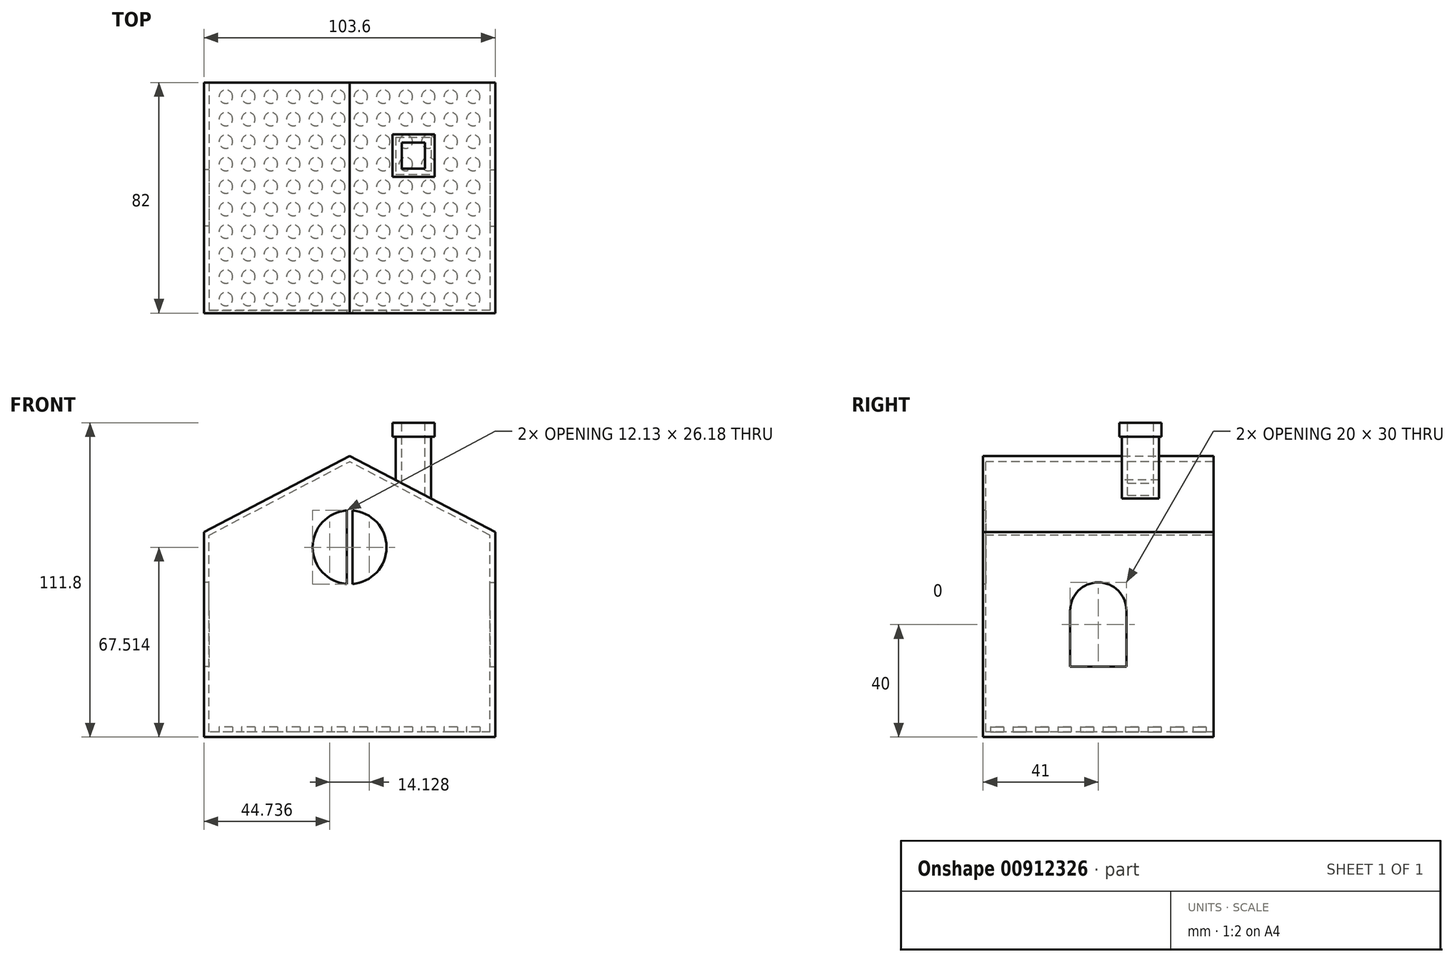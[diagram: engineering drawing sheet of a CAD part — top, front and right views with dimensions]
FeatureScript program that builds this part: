
annotation { "Feature Type Name" : "Feature", "Feature Type Description" : "" }
export const myFeature = defineFeature(function(context is Context, id is Id, definition is map)
    precondition{}
    {
        {
            var Q0;
            Q0=qCreatedBy(makeId("Front.planeOp"),FACE);
            var sketch = newSketch(context, id + "F0", { "sketchPlane" : qUnion([Q0])});
            skLineSegment(sketch, "E0", {"start": v(0, 0) * mm, "end": v(50, 0) * mm});
            skLineSegment(sketch, "E1", {"start": v(50, 0) * mm, "end": v(50, 70) * mm});
            skLineSegment(sketch, "E2", {"start": v(50, 70) * mm, "end": v(0, 96.17) * mm});
            skLineSegment(sketch, "E3", {"start": v(0, 96.17) * mm, "end": v(0, 0) * mm, "construction": true});
            skLineSegment(sketch, "E4.MirrorCS", {"start": v(-50, 70) * mm, "end": v(0, 96.17) * mm});
            skLineSegment(sketch, "E5.MirrorCS", {"start": v(-50, 0) * mm, "end": v(-50, 70) * mm});
            skLineSegment(sketch, "E6.MirrorCS", {"start": v(0, 0) * mm, "end": v(-50, 0) * mm});
            skLineSegment(sketch, "E7.0", {"start": v(0, -1.8) * mm, "end": v(51.8, -1.8) * mm});
            skLineSegment(sketch, "E7.1", {"start": v(51.8, 71.09) * mm, "end": v(0, 98.2) * mm});
            skLineSegment(sketch, "E7.2", {"start": v(-51.8, 71.09) * mm, "end": v(0, 98.2) * mm});
            skLineSegment(sketch, "E7.3", {"start": v(51.8, -1.8) * mm, "end": v(51.8, 71.09) * mm});
            skLineSegment(sketch, "E7.4", {"start": v(-51.8, -1.8) * mm, "end": v(-51.8, 71.09) * mm});
            skLineSegment(sketch, "E7.5", {"start": v(0, -1.8) * mm, "end": v(-51.8, -1.8) * mm});
            skSolve(sketch);
        }
        {
            var Q0;
            Q0=makeQuery(id+"F0.imprint","IMPRINT",FACE,{"disambiguationData":[TD([[makeQuery(id+"F0.imprint","IMPRINT",EDGE,{"derivedFrom":sQuery(id+"F0.wireOp",EDGE,"E0")}),-1.0]])]});
            var Q1;
            Q1=makeQuery(id+"F0.imprint","IMPRINT",FACE,{"disambiguationData":[TD([[makeQuery(id+"F0.imprint","IMPRINT",EDGE,{"derivedFrom":sQuery(id+"F0.wireOp",EDGE,"E0")}),1.0]])]});
            extrude(context, id + "F1", {"entities" : qUnion([Q0, Q1]), "endBound" : BoundingType.SYMMETRIC, "depth" : 82 * mm, "offsetDistance" : 25 * mm});
        }
        {
            var Q0;
            Q0=makeQuery(id+"F1.opExtrude","SWEPT_FACE",FACE,{"disambiguationData":[OSD([sQuery(id+"F0.wireOp",EDGE,"E7.4")])]});
            var sketch = newSketch(context, id + "F2", { "sketchPlane" : qUnion([Q0])});
            skLineSegment(sketch, "E8.top", {"start": v(-10, 23.2) * mm, "end": v(10, 23.2) * mm});
            skLineSegment(sketch, "E8.left", {"start": v(-10, 43.2) * mm, "end": v(-10, 23.2) * mm});
            skLineSegment(sketch, "E8.right", {"start": v(10, 43.2) * mm, "end": v(10, 23.2) * mm});
            skArc(sketch, "E9", {"start": v(10, 43.2) * mm, "mid": v(0, 53.2) * mm, "end": v(-10, 43.2) * mm});
            skSolve(sketch);
        }
        {
            var Q0;
            Q0=makeQuery(id+"F2.imprint","IMPRINT",FACE,{"disambiguationData":[TD([[makeQuery(id+"F2.imprint","IMPRINT",EDGE,{"derivedFrom":sQuery(id+"F2.wireOp",EDGE,"E8.bottom")}),-1.0]])]});
            var Q1;
            Q1=makeQuery(id+"F2.imprint","IMPRINT",FACE,{"disambiguationData":[TD([[makeQuery(id+"F2.imprint","IMPRINT",EDGE,{"derivedFrom":sQuery(id+"F2.wireOp",EDGE,"E8.top")}),1.0]])]});
            extrude(context, id + "F3", {"entities" : qUnion([Q0, Q1]), "operationType" : NewBodyOperationType.REMOVE, "oppositeDirection" : true, "depth" : 25 * mm, "offsetDistance" : 25 * mm});
        }
        {
            var Q0;
            Q0=makeQuery(id+"F1.opExtrude","SWEPT_FACE",FACE,{"disambiguationData":[OSD([sQuery(id+"F0.wireOp",EDGE,"E7.3")])]});
            var sketch = newSketch(context, id + "F4", { "sketchPlane" : qUnion([Q0])});
            skLineSegment(sketch, "E10.top", {"start": v(-10, 23.2) * mm, "end": v(10, 23.2) * mm});
            skLineSegment(sketch, "E10.left", {"start": v(-10, 43.2) * mm, "end": v(-10, 23.2) * mm});
            skLineSegment(sketch, "E10.right", {"start": v(10, 43.2) * mm, "end": v(10, 23.2) * mm});
            skArc(sketch, "E11", {"start": v(10, 43.2) * mm, "mid": v(0, 53.2) * mm, "end": v(-10, 43.2) * mm});
            skSolve(sketch);
        }
        {
            var Q0;
            Q0=makeQuery(id+"F4.imprint","IMPRINT",FACE,{"disambiguationData":[TD([[makeQuery(id+"F4.imprint","IMPRINT",EDGE,{"derivedFrom":sQuery(id+"F4.wireOp",EDGE,"E10.top")}),1.0]])]});
            extrude(context, id + "F5", {"entities" : qUnion([Q0]), "operationType" : NewBodyOperationType.REMOVE, "oppositeDirection" : true, "depth" : 25 * mm, "offsetDistance" : 25 * mm});
        }
        {
            var Q0;
            Q0=qCreatedBy(makeId("Front.planeOp"),FACE);
            cPlane(context, id + "F6", {"entities" : qUnion([Q0]), "cplaneType" : CPlaneType.OFFSET, "offset" : 40 * mm, "width" : 150 * mm, "height" : 150 * mm});
        }
        {
            var Q0;
            Q0=makeQuery(id+"F0.imprint","IMPRINT",FACE,{"disambiguationData":[TD([[makeQuery(id+"F0.imprint","IMPRINT",EDGE,{"derivedFrom":sQuery(id+"F0.wireOp",EDGE,"E0")}),1.0]])]});
            extrude(context, id + "F7", {"entities" : qUnion([Q0]), "operationType" : NewBodyOperationType.REMOVE, "oppositeDirection" : true, "depth" : 41 * mm, "offsetDistance" : 25 * mm});
        }
        {
            var Q0;
            Q0=makeQuery(id+"F0.imprint","IMPRINT",FACE,{"disambiguationData":[TD([[makeQuery(id+"F0.imprint","IMPRINT",EDGE,{"derivedFrom":sQuery(id+"F0.wireOp",EDGE,"E0")}),1.0]])]});
            extrude(context, id + "F8", {"entities" : qUnion([Q0]), "operationType" : NewBodyOperationType.REMOVE, "depth" : 40 * mm, "offsetDistance" : 25 * mm});
        }
        {
            var Q0;
            Q0=makeQuery(id+"F1.opExtrude","CAP_FACE",FACE,{"disambiguationData":[OSD([sQuery(id+"F0.wireOp",EDGE,"E7.0"),sQuery(id+"F0.wireOp",EDGE,"E7.1"),sQuery(id+"F0.wireOp",EDGE,"E7.2"),sQuery(id+"F0.wireOp",EDGE,"E7.3"),sQuery(id+"F0.wireOp",EDGE,"E7.4"),sQuery(id+"F0.wireOp",EDGE,"E7.5")])],"isStart":false});
            var sketch = newSketch(context, id + "F9", { "sketchPlane" : qUnion([Q0])});
            skCircle(sketch, "E12", {"center": v(0, 65.71) * mm, "radius": 13.13 * mm});
            skLineSegment(sketch, "E13", {"start": v(-13.13, 65.96) * mm, "end": v(13.13, 65.96) * mm, "construction": true});
            skLineSegment(sketch, "E14", {"start": v(0, 78.84) * mm, "end": v(0, 52.59) * mm, "construction": true});
            skLineSegment(sketch, "E15.0", {"start": v(-1, 78.84) * mm, "end": v(-1, 52.59) * mm});
            skLineSegment(sketch, "E16.0", {"start": v(1, 78.84) * mm, "end": v(1, 52.59) * mm});
            skSolve(sketch);
        }
        {
            var Q0;
            Q0=qCreatedBy(makeId("Top.planeOp"),FACE);
            var sketch = newSketch(context, id + "F10", { "sketchPlane" : qUnion([Q0])});
            skCircle(sketch, "E17", {"center": v(-44, 36) * mm, "radius": 2.4 * mm});
            skCircle(sketch, "E18.0.1.0", {"center": v(-44, 28) * mm, "radius": 2.4 * mm});
            skCircle(sketch, "E18.0.2.0", {"center": v(-44, 20) * mm, "radius": 2.4 * mm});
            skCircle(sketch, "E18.0.3.0", {"center": v(-44, 12) * mm, "radius": 2.4 * mm});
            skCircle(sketch, "E18.0.4.0", {"center": v(-44, 4) * mm, "radius": 2.4 * mm});
            skCircle(sketch, "E18.0.5.0", {"center": v(-44, -4) * mm, "radius": 2.4 * mm});
            skCircle(sketch, "E18.0.6.0", {"center": v(-44, -12) * mm, "radius": 2.4 * mm});
            skCircle(sketch, "E18.0.7.0", {"center": v(-44, -20) * mm, "radius": 2.4 * mm});
            skCircle(sketch, "E18.0.8.0", {"center": v(-44, -28) * mm, "radius": 2.4 * mm});
            skCircle(sketch, "E18.0.9.0", {"center": v(-44, -36) * mm, "radius": 2.4 * mm});
            skCircle(sketch, "E18.1.0.0", {"center": v(-36, 36) * mm, "radius": 2.4 * mm});
            skCircle(sketch, "E18.1.1.0", {"center": v(-36, 28) * mm, "radius": 2.4 * mm});
            skCircle(sketch, "E18.1.2.0", {"center": v(-36, 20) * mm, "radius": 2.4 * mm});
            skCircle(sketch, "E18.1.3.0", {"center": v(-36, 12) * mm, "radius": 2.4 * mm});
            skCircle(sketch, "E18.1.4.0", {"center": v(-36, 4) * mm, "radius": 2.4 * mm});
            skCircle(sketch, "E18.1.5.0", {"center": v(-36, -4) * mm, "radius": 2.4 * mm});
            skCircle(sketch, "E18.1.6.0", {"center": v(-36, -12) * mm, "radius": 2.4 * mm});
            skCircle(sketch, "E18.1.7.0", {"center": v(-36, -20) * mm, "radius": 2.4 * mm});
            skCircle(sketch, "E18.1.8.0", {"center": v(-36, -28) * mm, "radius": 2.4 * mm});
            skCircle(sketch, "E18.1.9.0", {"center": v(-36, -36) * mm, "radius": 2.4 * mm});
            skCircle(sketch, "E18.2.0.0", {"center": v(-28, 36) * mm, "radius": 2.4 * mm});
            skCircle(sketch, "E18.2.1.0", {"center": v(-28, 28) * mm, "radius": 2.4 * mm});
            skCircle(sketch, "E18.2.2.0", {"center": v(-28, 20) * mm, "radius": 2.4 * mm});
            skCircle(sketch, "E18.2.3.0", {"center": v(-28, 12) * mm, "radius": 2.4 * mm});
            skCircle(sketch, "E18.2.4.0", {"center": v(-28, 4) * mm, "radius": 2.4 * mm});
            skCircle(sketch, "E18.2.5.0", {"center": v(-28, -4) * mm, "radius": 2.4 * mm});
            skCircle(sketch, "E18.2.6.0", {"center": v(-28, -12) * mm, "radius": 2.4 * mm});
            skCircle(sketch, "E18.2.7.0", {"center": v(-28, -20) * mm, "radius": 2.4 * mm});
            skCircle(sketch, "E18.2.8.0", {"center": v(-28, -28) * mm, "radius": 2.4 * mm});
            skCircle(sketch, "E18.2.9.0", {"center": v(-28, -36) * mm, "radius": 2.4 * mm});
            skCircle(sketch, "E18.3.0.0", {"center": v(-20, 36) * mm, "radius": 2.4 * mm});
            skCircle(sketch, "E18.3.1.0", {"center": v(-20, 28) * mm, "radius": 2.4 * mm});
            skCircle(sketch, "E18.3.2.0", {"center": v(-20, 20) * mm, "radius": 2.4 * mm});
            skCircle(sketch, "E18.3.3.0", {"center": v(-20, 12) * mm, "radius": 2.4 * mm});
            skCircle(sketch, "E18.3.4.0", {"center": v(-20, 4) * mm, "radius": 2.4 * mm});
            skCircle(sketch, "E18.3.5.0", {"center": v(-20, -4) * mm, "radius": 2.4 * mm});
            skCircle(sketch, "E18.3.6.0", {"center": v(-20, -12) * mm, "radius": 2.4 * mm});
            skCircle(sketch, "E18.3.7.0", {"center": v(-20, -20) * mm, "radius": 2.4 * mm});
            skCircle(sketch, "E18.3.8.0", {"center": v(-20, -28) * mm, "radius": 2.4 * mm});
            skCircle(sketch, "E18.3.9.0", {"center": v(-20, -36) * mm, "radius": 2.4 * mm});
            skCircle(sketch, "E18.4.0.0", {"center": v(-12, 36) * mm, "radius": 2.4 * mm});
            skCircle(sketch, "E18.4.1.0", {"center": v(-12, 28) * mm, "radius": 2.4 * mm});
            skCircle(sketch, "E18.4.2.0", {"center": v(-12, 20) * mm, "radius": 2.4 * mm});
            skCircle(sketch, "E18.4.3.0", {"center": v(-12, 12) * mm, "radius": 2.4 * mm});
            skCircle(sketch, "E18.4.4.0", {"center": v(-12, 4) * mm, "radius": 2.4 * mm});
            skCircle(sketch, "E18.4.5.0", {"center": v(-12, -4) * mm, "radius": 2.4 * mm});
            skCircle(sketch, "E18.4.6.0", {"center": v(-12, -12) * mm, "radius": 2.4 * mm});
            skCircle(sketch, "E18.4.7.0", {"center": v(-12, -20) * mm, "radius": 2.4 * mm});
            skCircle(sketch, "E18.4.8.0", {"center": v(-12, -28) * mm, "radius": 2.4 * mm});
            skCircle(sketch, "E18.4.9.0", {"center": v(-12, -36) * mm, "radius": 2.4 * mm});
            skCircle(sketch, "E18.5.0.0", {"center": v(-4, 36) * mm, "radius": 2.4 * mm});
            skCircle(sketch, "E18.5.1.0", {"center": v(-4, 28) * mm, "radius": 2.4 * mm});
            skCircle(sketch, "E18.5.2.0", {"center": v(-4, 20) * mm, "radius": 2.4 * mm});
            skCircle(sketch, "E18.5.3.0", {"center": v(-4, 12) * mm, "radius": 2.4 * mm});
            skCircle(sketch, "E18.5.4.0", {"center": v(-4, 4) * mm, "radius": 2.4 * mm});
            skCircle(sketch, "E18.5.5.0", {"center": v(-4, -4) * mm, "radius": 2.4 * mm});
            skCircle(sketch, "E18.5.6.0", {"center": v(-4, -12) * mm, "radius": 2.4 * mm});
            skCircle(sketch, "E18.5.7.0", {"center": v(-4, -20) * mm, "radius": 2.4 * mm});
            skCircle(sketch, "E18.5.8.0", {"center": v(-4, -28) * mm, "radius": 2.4 * mm});
            skCircle(sketch, "E18.5.9.0", {"center": v(-4, -36) * mm, "radius": 2.4 * mm});
            skCircle(sketch, "E18.6.0.0", {"center": v(4, 36) * mm, "radius": 2.4 * mm});
            skCircle(sketch, "E18.6.1.0", {"center": v(4, 28) * mm, "radius": 2.4 * mm});
            skCircle(sketch, "E18.6.2.0", {"center": v(4, 20) * mm, "radius": 2.4 * mm});
            skCircle(sketch, "E18.6.3.0", {"center": v(4, 12) * mm, "radius": 2.4 * mm});
            skCircle(sketch, "E18.6.4.0", {"center": v(4, 4) * mm, "radius": 2.4 * mm});
            skCircle(sketch, "E18.6.5.0", {"center": v(4, -4) * mm, "radius": 2.4 * mm});
            skCircle(sketch, "E18.6.6.0", {"center": v(4, -12) * mm, "radius": 2.4 * mm});
            skCircle(sketch, "E18.6.7.0", {"center": v(4, -20) * mm, "radius": 2.4 * mm});
            skCircle(sketch, "E18.6.8.0", {"center": v(4, -28) * mm, "radius": 2.4 * mm});
            skCircle(sketch, "E18.6.9.0", {"center": v(4, -36) * mm, "radius": 2.4 * mm});
            skCircle(sketch, "E18.7.0.0", {"center": v(12, 36) * mm, "radius": 2.4 * mm});
            skCircle(sketch, "E18.7.1.0", {"center": v(12, 28) * mm, "radius": 2.4 * mm});
            skCircle(sketch, "E18.7.2.0", {"center": v(12, 20) * mm, "radius": 2.4 * mm});
            skCircle(sketch, "E18.7.3.0", {"center": v(12, 12) * mm, "radius": 2.4 * mm});
            skCircle(sketch, "E18.7.4.0", {"center": v(12, 4) * mm, "radius": 2.4 * mm});
            skCircle(sketch, "E18.7.5.0", {"center": v(12, -4) * mm, "radius": 2.4 * mm});
            skCircle(sketch, "E18.7.6.0", {"center": v(12, -12) * mm, "radius": 2.4 * mm});
            skCircle(sketch, "E18.7.7.0", {"center": v(12, -20) * mm, "radius": 2.4 * mm});
            skCircle(sketch, "E18.7.8.0", {"center": v(12, -28) * mm, "radius": 2.4 * mm});
            skCircle(sketch, "E18.7.9.0", {"center": v(12, -36) * mm, "radius": 2.4 * mm});
            skCircle(sketch, "E18.8.0.0", {"center": v(20, 36) * mm, "radius": 2.4 * mm});
            skCircle(sketch, "E18.8.1.0", {"center": v(20, 28) * mm, "radius": 2.4 * mm});
            skCircle(sketch, "E18.8.2.0", {"center": v(20, 20) * mm, "radius": 2.4 * mm});
            skCircle(sketch, "E18.8.3.0", {"center": v(20, 12) * mm, "radius": 2.4 * mm});
            skCircle(sketch, "E18.8.4.0", {"center": v(20, 4) * mm, "radius": 2.4 * mm});
            skCircle(sketch, "E18.8.5.0", {"center": v(20, -4) * mm, "radius": 2.4 * mm});
            skCircle(sketch, "E18.8.6.0", {"center": v(20, -12) * mm, "radius": 2.4 * mm});
            skCircle(sketch, "E18.8.7.0", {"center": v(20, -20) * mm, "radius": 2.4 * mm});
            skCircle(sketch, "E18.8.8.0", {"center": v(20, -28) * mm, "radius": 2.4 * mm});
            skCircle(sketch, "E18.8.9.0", {"center": v(20, -36) * mm, "radius": 2.4 * mm});
            skCircle(sketch, "E18.9.0.0", {"center": v(28, 36) * mm, "radius": 2.4 * mm});
            skCircle(sketch, "E18.9.1.0", {"center": v(28, 28) * mm, "radius": 2.4 * mm});
            skCircle(sketch, "E18.9.2.0", {"center": v(28, 20) * mm, "radius": 2.4 * mm});
            skCircle(sketch, "E18.9.3.0", {"center": v(28, 12) * mm, "radius": 2.4 * mm});
            skCircle(sketch, "E18.9.4.0", {"center": v(28, 4) * mm, "radius": 2.4 * mm});
            skCircle(sketch, "E18.9.5.0", {"center": v(28, -4) * mm, "radius": 2.4 * mm});
            skCircle(sketch, "E18.9.6.0", {"center": v(28, -12) * mm, "radius": 2.4 * mm});
            skCircle(sketch, "E18.9.7.0", {"center": v(28, -20) * mm, "radius": 2.4 * mm});
            skCircle(sketch, "E18.9.8.0", {"center": v(28, -28) * mm, "radius": 2.4 * mm});
            skCircle(sketch, "E18.9.9.0", {"center": v(28, -36) * mm, "radius": 2.4 * mm});
            skCircle(sketch, "E18.10.0.0", {"center": v(36, 36) * mm, "radius": 2.4 * mm});
            skCircle(sketch, "E18.10.1.0", {"center": v(36, 28) * mm, "radius": 2.4 * mm});
            skCircle(sketch, "E18.10.2.0", {"center": v(36, 20) * mm, "radius": 2.4 * mm});
            skCircle(sketch, "E18.10.3.0", {"center": v(36, 12) * mm, "radius": 2.4 * mm});
            skCircle(sketch, "E18.10.4.0", {"center": v(36, 4) * mm, "radius": 2.4 * mm});
            skCircle(sketch, "E18.10.5.0", {"center": v(36, -4) * mm, "radius": 2.4 * mm});
            skCircle(sketch, "E18.10.6.0", {"center": v(36, -12) * mm, "radius": 2.4 * mm});
            skCircle(sketch, "E18.10.7.0", {"center": v(36, -20) * mm, "radius": 2.4 * mm});
            skCircle(sketch, "E18.10.8.0", {"center": v(36, -28) * mm, "radius": 2.4 * mm});
            skCircle(sketch, "E18.10.9.0", {"center": v(36, -36) * mm, "radius": 2.4 * mm});
            skCircle(sketch, "E18.11.0.0", {"center": v(44, 36) * mm, "radius": 2.4 * mm});
            skCircle(sketch, "E18.11.1.0", {"center": v(44, 28) * mm, "radius": 2.4 * mm});
            skCircle(sketch, "E18.11.2.0", {"center": v(44, 20) * mm, "radius": 2.4 * mm});
            skCircle(sketch, "E18.11.3.0", {"center": v(44, 12) * mm, "radius": 2.4 * mm});
            skCircle(sketch, "E18.11.4.0", {"center": v(44, 4) * mm, "radius": 2.4 * mm});
            skCircle(sketch, "E18.11.5.0", {"center": v(44, -4) * mm, "radius": 2.4 * mm});
            skCircle(sketch, "E18.11.6.0", {"center": v(44, -12) * mm, "radius": 2.4 * mm});
            skCircle(sketch, "E18.11.7.0", {"center": v(44, -20) * mm, "radius": 2.4 * mm});
            skCircle(sketch, "E18.11.8.0", {"center": v(44, -28) * mm, "radius": 2.4 * mm});
            skCircle(sketch, "E18.11.9.0", {"center": v(44, -36) * mm, "radius": 2.4 * mm});
            skLineSegment(sketch, "E18.direction1", {"start": v(-44, 36) * mm, "end": v(-36, 36) * mm, "construction": true});
            skLineSegment(sketch, "E18.direction2", {"start": v(-44, 36) * mm, "end": v(-44, 28) * mm, "construction": true});
            skSolve(sketch);
        }
        {
            var Q0;
            Q0 = qSketchRegion(id + "F10", true);
            extrude(context, id + "F11", {"entities" : qUnion([Q0]), "operationType" : NewBodyOperationType.ADD, "depth" : 1.8 * mm, "offsetDistance" : 25 * mm});
        }
        {
            var Q0;
            {var subQ0=sQuery(id+"F9.wireOp",EDGE,"E15.0");var subQ1=sQuery(id+"F9.wireOp",EDGE,"E12");var subQ2=makeQuery(id+"F9.imprint","INTERSECT",VERTEX,{"disambiguationData":[OD(0.0)],"derivedFrom":[subQ1,subQ0]});Q0=makeQuery(id+"F9.imprint","IMPRINT",FACE,{"disambiguationData":[TD([[makeQuery(id+"F9.imprint","IMPRINT",EDGE,{"disambiguationData":[TD([[subQ2,-1.0]])],"derivedFrom":subQ1}),1.0]])]});}
            var Q1;
            {var subQ0=sQuery(id+"F9.wireOp",EDGE,"E16.0");var subQ1=sQuery(id+"F9.wireOp",EDGE,"E12");var subQ2=makeQuery(id+"F9.imprint","INTERSECT",VERTEX,{"disambiguationData":[OD(0.0)],"derivedFrom":[subQ1,subQ0]});Q1=makeQuery(id+"F9.imprint","IMPRINT",FACE,{"disambiguationData":[TD([[makeQuery(id+"F9.imprint","IMPRINT",EDGE,{"disambiguationData":[TD([[subQ2,1.0]])],"derivedFrom":subQ1}),1.0]])]});}
            extrude(context, id + "F12", {"entities" : qUnion([Q0, Q1]), "operationType" : NewBodyOperationType.REMOVE, "oppositeDirection" : true, "depth" : 25 * mm, "offsetDistance" : 25 * mm});
        }
        {
            var Q0;
            Q0=qCreatedBy(makeId("Top.planeOp"),FACE);
            cPlane(context, id + "F13", {"entities" : qUnion([Q0]), "cplaneType" : CPlaneType.OFFSET, "offset" : 110 * mm, "width" : 150 * mm, "height" : 150 * mm});
        }
        {
            var Q0;
            Q0=qCreatedBy(id+"F13.planeOp",FACE);
            var sketch = newSketch(context, id + "F14", { "sketchPlane" : qUnion([Q0])});
            skLineSegment(sketch, "E19.bottom", {"start": v(16.41, 21.63) * mm, "end": v(29.03, 21.63) * mm});
            skLineSegment(sketch, "E19.top", {"start": v(16.41, 8.43) * mm, "end": v(29.03, 8.43) * mm});
            skLineSegment(sketch, "E19.left", {"start": v(16.41, 21.63) * mm, "end": v(16.41, 8.43) * mm});
            skLineSegment(sketch, "E19.right", {"start": v(29.03, 21.63) * mm, "end": v(29.03, 8.43) * mm});
            skLineSegment(sketch, "E20", {"start": v(16.41, 15.03) * mm, "end": v(29.03, 15.03) * mm, "construction": true});
            skLineSegment(sketch, "E21", {"start": v(22.72, 21.63) * mm, "end": v(22.72, 8.43) * mm, "construction": true});
            skLineSegment(sketch, "E22.bottom", {"start": v(26.86, 10.4) * mm, "end": v(18.58, 10.4) * mm});
            skLineSegment(sketch, "E22.top", {"start": v(26.86, 19.66) * mm, "end": v(18.58, 19.66) * mm});
            skLineSegment(sketch, "E22.left", {"start": v(26.86, 10.4) * mm, "end": v(26.86, 19.66) * mm});
            skLineSegment(sketch, "E22.right", {"start": v(18.58, 10.4) * mm, "end": v(18.58, 19.66) * mm});
            skPoint(sketch, "E22.middle", {"position": v(22.72, 15.03) * mm});
            skLineSegment(sketch, "E23.bottom", {"start": v(30.22, 7.53) * mm, "end": v(15.21, 7.53) * mm});
            skLineSegment(sketch, "E23.top", {"start": v(30.22, 22.53) * mm, "end": v(15.21, 22.53) * mm});
            skLineSegment(sketch, "E23.left", {"start": v(30.22, 7.53) * mm, "end": v(30.22, 22.53) * mm});
            skLineSegment(sketch, "E23.right", {"start": v(15.21, 7.53) * mm, "end": v(15.21, 22.53) * mm});
            skSolve(sketch);
        }
        {
            var Q0;
            Q0=makeQuery(id+"F14.imprint","IMPRINT",FACE,{"disambiguationData":[TD([[makeQuery(id+"F14.imprint","IMPRINT",EDGE,{"derivedFrom":sQuery(id+"F14.wireOp",EDGE,"E19.bottom")}),-1.0]])]});
            extrude(context, id + "F15", {"entities" : qUnion([Q0]), "operationType" : NewBodyOperationType.ADD, "endBound" : BoundingType.UP_TO_NEXT, "oppositeDirection" : true, "depth" : 25 * mm, "offsetDistance" : 25 * mm});
        }
        {
            var Q0;
            Q0=makeQuery(id+"F14.imprint","IMPRINT",FACE,{"disambiguationData":[TD([[makeQuery(id+"F14.imprint","IMPRINT",EDGE,{"derivedFrom":sQuery(id+"F14.wireOp",EDGE,"E19.bottom")}),1.0]])]});
            extrude(context, id + "F16", {"entities" : qUnion([Q0]), "operationType" : NewBodyOperationType.ADD, "oppositeDirection" : true, "depth" : 5 * mm, "offsetDistance" : 25 * mm});
        }
    });
